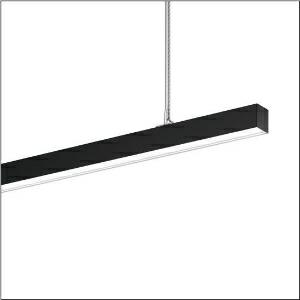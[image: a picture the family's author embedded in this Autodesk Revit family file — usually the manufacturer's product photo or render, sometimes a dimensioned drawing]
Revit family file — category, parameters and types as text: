
# Revit family: silica_r__21_51mx30db35bb_2e66
name_source: partatom
category: Lighting Fixtures
units: mm (PartAtom-declared; Revit-internal decimal feet)

## family parameters
Cut with Voids When Loaded = No
Host = Face
Light Source = No
Part Type = Normal
Room Calculation Point = No
Round Connector Dimension = Use Diameter
Shared = No

## types (1)
- --- (1 x LED, 5260 lm, 34.1 W, 3000K)
    Apparent Load = 34 VA
    CIE Flux Codes = 47 79 96 57 100
    Color Rendering = 80
    Color Temperature = 3000K
    Default Elevation = 1800 mm
    Description = Silica® 21, office luminaire, primary optical cover: cover, of PMMA, opal, light emission: direct/indirect distribution, primary light characteristic: symmetric, installation type: suspended mounting, LED, rated luminous flux: 5.260lm, luminous efficacy: 154lm/W, light colour: 830, colour temperature: 3000K, control gear: DALI 2, with terminal, 3+2-pole, max. 2.5mm², mains connection: 220..240V, AC, 50/60Hz, rated input power: 34.1W, luminaire housing, of aluminium, matt jet black (RAL 9005), length: 1.504mm, width: 53mm, height: 53mm, protection rating (complete): IP20, insulation class (complete): insulation class I (protective earthing), certification: CE, permissible operating ambient temperature: 0..+35°C, standard: EN 50419, packaging unit: 1 piece
    Height = 53 mm
    Lamp = 1 x LED
    Lamp Light Flux = 5260 lm
    Lamp Power = 34.1 W
    Lamp count = 1
    Length = 1504 mm
    Luminous efficacy = 154 lm/W
    Manufacturer = Siteco
    ModVariant = No
    Model = 51MX30DB35BB
    Mounting Place = Ceiling
    Mounting Type = Pendant
    Number of Poles = 1
    OnlyDefault = Yes
    Power Factor = 1
    Product Name = Silica® 21
    Product group = office luminaire | ceiling pendant
    ProductGroupID = 904
    Protection Class = Protection class I
    Protection Degree = IP 20
    RLX_Detail_Level = 1
    RLX_Emergency_Light_Flux = 0 lm
    RLX_Emergency_Type = 0
    RLX_Emergency_Type_DB = No
    RlxData = <blob elided: 26153 chars, md5=0970dbe8>
    Socket = socket
    Standby Power = 0 W
    System Light Flux = 5260 lm
    System Power = 34 W
    Type Comments = factory setting: luminous flux: 100 % | dim-lin: 254 | 233 mA
    Type Image = l_1335856.jpg
    URL = http://relux.com
    VarID = @adj_116978
    Voltage = 0 V
    Weight = 0.00 kg
    Width = 53 mm

## geometry (parser evidence)
native form markers: Blend x4, Sweep x14
no freeform markers — native parametric forms only
